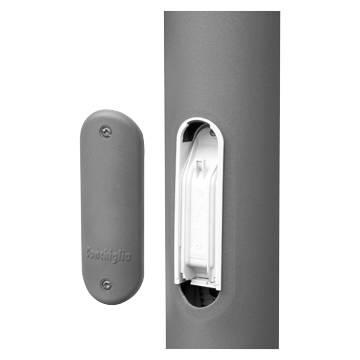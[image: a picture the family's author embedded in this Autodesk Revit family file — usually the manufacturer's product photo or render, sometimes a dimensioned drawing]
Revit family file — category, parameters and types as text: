
# Revit family: Lighting-Stradale-GEWISS-STREET[O3]-PALI_CONICI
name_source: partatom
category: Apparecchi per illuminazione
units: mm (PartAtom-declared; Revit-internal decimal feet)

## family parameters
Condiviso = No
Host = Superficie
Numero OmniClass = 23.80.00.00
Punto di calcolo locali = No
Quota connettore circolare = Usa diametro
Sorgente d'illuminazione = No
Taglio con vuoti quando caricato = No
Tipo di parte = Normale
Titolo OmniClass = Electric Power and Lighting

## types (1)
- Lighting-Stradale-GEWISS-STREET[O3]-PALI_CONICI
    Altezza palo = 9800 mm  [stored 32.1522 ft]
    Catalogo = LIGHTING
    Catalogo Serie = STREET [O3]
    Codice EAN = 8011564782594
    Codice Electrocod = 240
    Colore = Grigio grafite
    Descrizione = STREET PALO CONICO 9,8m GRIGIO GRAFITE
    Diametro = 60 mm  [stored 0.19685 ft]
    Diametro base (mm) = 158
    Diametro inferiore = 158 mm  [stored 0.518373 ft]
    Diametro sommità (mm) = 60
    Finitura = Verniciato
    IDF = 6a85b173-ae80-4b60-8f8b-d13c22feb59a
    IDT = d3b2aa7b-33ea-43be-8ddf-58a48c27c07e
    Immagine tipo = GW84096.jpg
    Interramento (m) = 0,8
    Lunghezza totale (m) = 9,8
    Materiale = Acciaio zincato
    Modello = GW87593
    Palo = <Per categoria>
    Peso (kg) = 107
    Peso (kg): = 107
    Produttore = GEWISS S.p.A.
    Prospetto di default = 1219 mm
    SEO = Palo
    Scheda Tecnica = https://www.gewiss.com
    Tipo: = Conico
    URL = https://www.gewiss.com
    Versione file RFA = 20.11

note: [stored X ft] marks values corroborated as IEEE doubles in the binary element streams (Revit-internal decimal feet)

## geometry (parser evidence)
native form markers: Blend x2
no freeform markers — native parametric forms only
